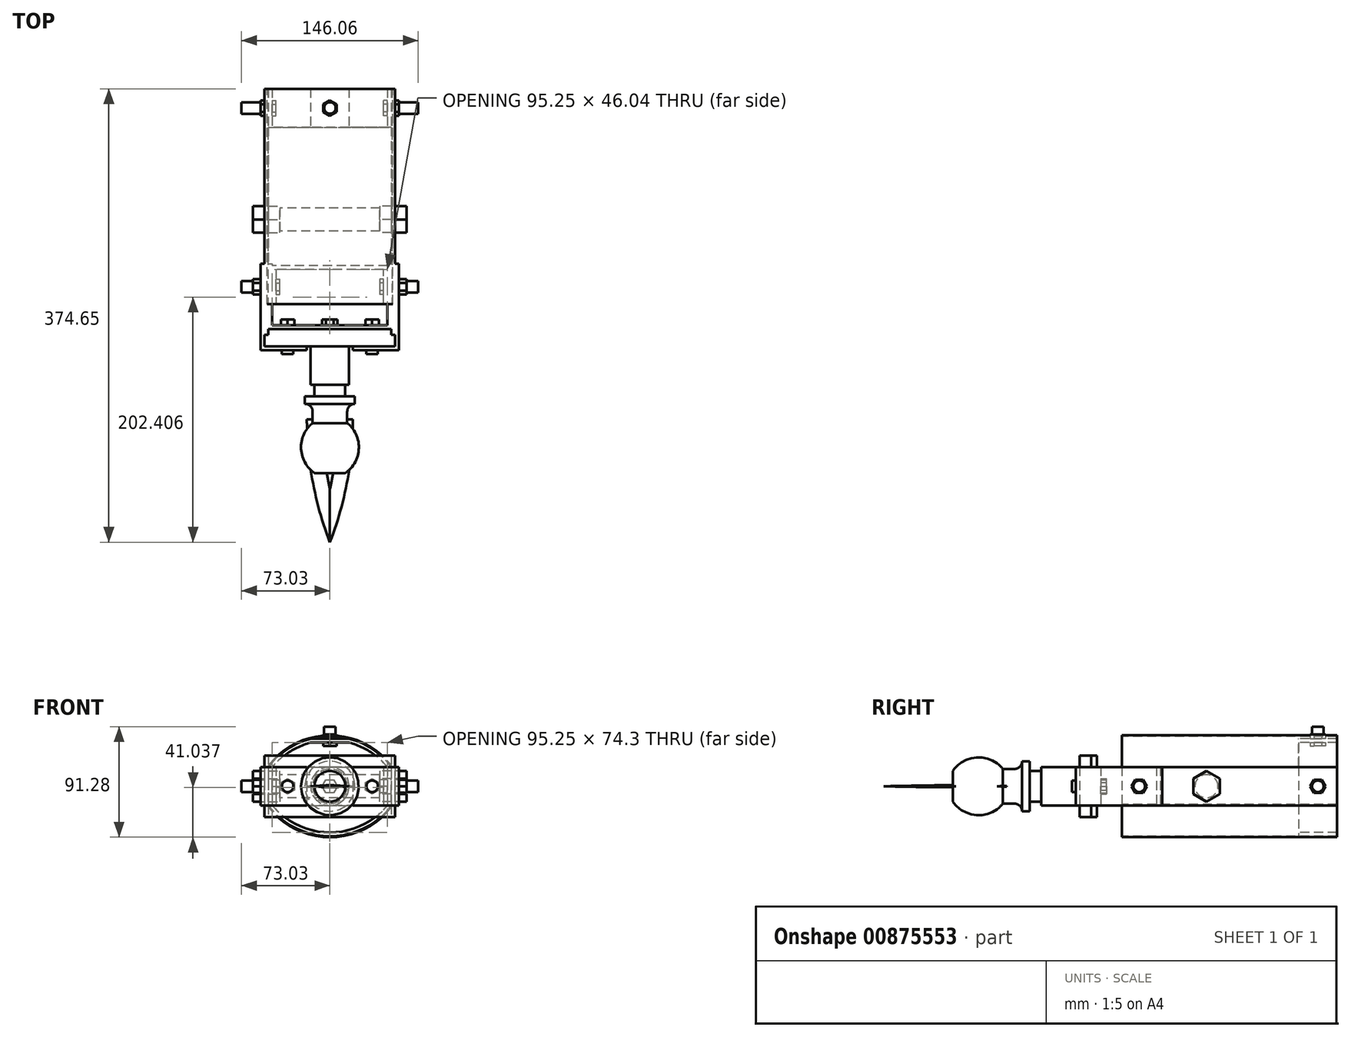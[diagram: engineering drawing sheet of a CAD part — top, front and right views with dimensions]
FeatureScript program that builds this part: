
annotation { "Feature Type Name" : "Feature", "Feature Type Description" : "" }
export const myFeature = defineFeature(function(context is Context, id is Id, definition is map)
    precondition{}
    {
        {
            var Q0;
            Q0=qCreatedBy(makeId("Right.planeOp"),FACE);
            var sketch = newSketch(context, id + "F0", { "sketchPlane" : qUnion([Q0])});
            skLineSegment(sketch, "E0.bottom", {"start": v(101.6, -15.88) * mm, "end": v(-101.6, -15.88) * mm});
            skLineSegment(sketch, "E0.top", {"start": v(101.6, 15.88) * mm, "end": v(-101.6, 15.88) * mm});
            skLineSegment(sketch, "E0.left", {"start": v(101.6, -15.88) * mm, "end": v(101.6, 15.87) * mm});
            skLineSegment(sketch, "E0.right", {"start": v(-101.6, -15.88) * mm, "end": v(-101.6, 15.87) * mm});
            skPoint(sketch, "E0.middle", {"position": v(0, 0) * mm});
            skSolve(sketch);
        }
        {
            var Q0;
            Q0 = qSketchRegion(id + "F0", true);
            extrude(context, id + "F1", {"entities" : qUnion([Q0]), "depth" : 53.97 * mm, "offsetDistance" : 25.4 * mm, "hasSecondDirection" : true, "secondDirectionOppositeDirection" : false, "secondDirectionDepth" : 50.8 * mm});
        }
        {
            var Q0;
            Q0=makeQuery(id+"F0.imprint","IMPRINT",FACE,{"disambiguationData":[TD([[makeQuery(id+"F0.imprint","IMPRINT",EDGE,{"derivedFrom":sQuery(id+"F0.wireOp",EDGE,"E0.bottom")}),-1.0]])]});
            extrude(context, id + "F2", {"entities" : qUnion([Q0]), "oppositeDirection" : true, "depth" : 53.97 * mm, "offsetDistance" : 25.4 * mm, "hasSecondDirection" : true, "secondDirectionOppositeDirection" : true, "secondDirectionDepth" : 50.8 * mm});
        }
        {
            var Q0;
            Q0=qCreatedBy(makeId("Front.planeOp"),FACE);
            var sketch = newSketch(context, id + "F3", { "sketchPlane" : qUnion([Q0])});
            skLineSegment(sketch, "E1", {"start": v(50.8, 15.88) * mm, "end": v(50.8, -15.88) * mm});
            skLineSegment(sketch, "E2", {"start": v(-50.8, 15.88) * mm, "end": v(-50.8, -15.88) * mm});
            skArc(sketch, "E3", {"start": v(-50.8, 15.88) * mm, "mid": v(-35.33, 30.54) * mm, "end": v(-15.88, 39.26) * mm});
            skArc(sketch, "E4", {"start": v(50.8, -15.88) * mm, "mid": v(0, -41.28) * mm, "end": v(-50.8, -15.88) * mm});
            skLineSegment(sketch, "E5", {"start": v(-47.62, 15.88) * mm, "end": v(-47.62, -15.88) * mm});
            skLineSegment(sketch, "E6", {"start": v(47.63, 15.88) * mm, "end": v(47.63, -15.88) * mm});
            skArc(sketch, "E7", {"start": v(-47.62, 15.87) * mm, "mid": v(-33.32, 28.46) * mm, "end": v(-15.88, 36.11) * mm});
            skArc(sketch, "E8", {"start": v(47.62, -15.87) * mm, "mid": v(0, -38.18) * mm, "end": v(-47.62, -15.88) * mm});
            skLineSegment(sketch, "E9", {"start": v(15.88, 39.26) * mm, "end": v(-15.88, 39.26) * mm});
            skLineSegment(sketch, "E10", {"start": v(15.88, 36.11) * mm, "end": v(-15.88, 36.11) * mm});
            skArc(sketch, "E11.trimOffspring", {"start": v(15.88, 39.26) * mm, "mid": v(35.33, 30.54) * mm, "end": v(50.8, 15.88) * mm});
            skArc(sketch, "E12.trimOffspring", {"start": v(15.87, 36.11) * mm, "mid": v(33.32, 28.46) * mm, "end": v(47.62, 15.87) * mm});
            skLineSegment(sketch, "E13", {"start": v(15.88, 39.26) * mm, "end": v(15.88, 37.7) * mm});
            skLineSegment(sketch, "E14", {"start": v(15.88, 37.7) * mm, "end": v(-15.88, 37.7) * mm});
            skLineSegment(sketch, "E15", {"start": v(-15.88, 37.7) * mm, "end": v(-15.88, 36.11) * mm});
            skSolve(sketch);
        }
        {
            var Q0;
            Q0=makeQuery(id+"F3.imprint","IMPRINT",FACE,{"disambiguationData":[TD([[makeQuery(id+"F3.imprint","IMPRINT",EDGE,{"derivedFrom":sQuery(id+"F3.wireOp",EDGE,"E1")}),-1.0]])]});
            extrude(context, id + "F4", {"entities" : qUnion([Q0]), "operationType" : NewBodyOperationType.ADD, "oppositeDirection" : true, "depth" : 101.6 * mm, "offsetDistance" : 25.4 * mm, "hasSecondDirection" : true, "secondDirectionOppositeDirection" : true, "secondDirectionDepth" : 69.85 * mm});
        }
        {
            var Q0;
            Q0=sQuery(id+"F3.wireOp",EDGE,"E15");
            var Q1;
            Q1=sQuery(id+"F3.wireOp",EDGE,"E14");
            var Q2;
            Q2=sQuery(id+"F3.wireOp",EDGE,"E13");
            extrude(context, id + "F5", {"bodyType" : ToolBodyType.SURFACE, "surfaceEntities" : qUnion([Q0, Q1, Q2]), "oppositeDirection" : true, "depth" : 101.73 * mm, "offsetDistance" : 25.4 * mm, "hasSecondDirection" : true, "secondDirectionOppositeDirection" : true, "secondDirectionDepth" : 69.72 * mm});
        }
        {
            var Q0;
            Q0=qCreatedBy(makeId("Top.planeOp"),FACE);
            var sketch = newSketch(context, id + "F6", { "sketchPlane" : qUnion([Q0])});
            skLineSegment(sketch, "E16.bottom", {"start": v(53.97, -106.36) * mm, "end": v(-53.98, -106.36) * mm});
            skLineSegment(sketch, "E16.top", {"start": v(53.98, -42.86) * mm, "end": v(-53.98, -42.86) * mm, "construction": true});
            skLineSegment(sketch, "E16.left", {"start": v(53.98, -106.36) * mm, "end": v(53.97, -42.86) * mm});
            skLineSegment(sketch, "E16.right", {"start": v(-53.98, -106.36) * mm, "end": v(-53.98, -42.86) * mm});
            skPoint(sketch, "E16.middle", {"position": v(0, -74.61) * mm});
            skLineSegment(sketch, "E17", {"start": v(-53.98, -42.86) * mm, "end": v(-57.15, -42.86) * mm});
            skLineSegment(sketch, "E18", {"start": v(-57.15, -42.86) * mm, "end": v(-57.15, -114.3) * mm});
            skLineSegment(sketch, "E19", {"start": v(-57.15, -114.3) * mm, "end": v(-19.05, -114.3) * mm});
            skLineSegment(sketch, "E20", {"start": v(57.15, -114.3) * mm, "end": v(57.15, -42.86) * mm});
            skLineSegment(sketch, "E21", {"start": v(57.15, -42.86) * mm, "end": v(53.98, -42.86) * mm});
            skLineSegment(sketch, "E22.bottom", {"start": v(-53.98, -106.36) * mm, "end": v(53.97, -106.36) * mm});
            skLineSegment(sketch, "E22.top", {"start": v(-53.98, -101.6) * mm, "end": v(53.97, -101.6) * mm});
            skLineSegment(sketch, "E22.left", {"start": v(-53.98, -106.36) * mm, "end": v(-53.98, -101.6) * mm});
            skLineSegment(sketch, "E22.right", {"start": v(53.98, -106.36) * mm, "end": v(53.98, -101.6) * mm});
            skLineSegment(sketch, "E23.bottom", {"start": v(-50.8, -101.6) * mm, "end": v(50.8, -101.6) * mm});
            skLineSegment(sketch, "E23.top", {"start": v(-50.8, -42.86) * mm, "end": v(50.8, -42.86) * mm, "construction": true});
            skLineSegment(sketch, "E23.left", {"start": v(-50.8, -101.6) * mm, "end": v(-50.8, -42.86) * mm});
            skLineSegment(sketch, "E23.right", {"start": v(50.8, -101.6) * mm, "end": v(50.8, -42.86) * mm});
            skLineSegment(sketch, "E24", {"start": v(-50.8, -42.86) * mm, "end": v(-47.63, -42.86) * mm});
            skLineSegment(sketch, "E25", {"start": v(-47.63, -42.86) * mm, "end": v(-47.62, -93.66) * mm});
            skLineSegment(sketch, "E26", {"start": v(-47.62, -93.66) * mm, "end": v(47.63, -93.66) * mm});
            skLineSegment(sketch, "E27", {"start": v(47.63, -93.66) * mm, "end": v(47.63, -42.86) * mm});
            skLineSegment(sketch, "E28", {"start": v(47.63, -42.86) * mm, "end": v(50.8, -42.86) * mm});
            skLineSegment(sketch, "E29.top", {"start": v(-50.8, -96.84) * mm, "end": v(50.8, -96.84) * mm});
            skLineSegment(sketch, "E29.left", {"start": v(-50.8, -101.6) * mm, "end": v(-50.8, -96.84) * mm});
            skLineSegment(sketch, "E29.right", {"start": v(50.8, -101.6) * mm, "end": v(50.8, -96.84) * mm});
            skLineSegment(sketch, "E30", {"start": v(-19.05, -111.12) * mm, "end": v(-19.05, -114.3) * mm});
            skLineSegment(sketch, "E31", {"start": v(19.05, -111.12) * mm, "end": v(19.05, -114.3) * mm});
            skLineSegment(sketch, "E32.trimOffspring", {"start": v(19.05, -114.3) * mm, "end": v(57.15, -114.3) * mm});
            skLineSegment(sketch, "E33", {"start": v(-53.98, -106.36) * mm, "end": v(-53.98, -111.13) * mm});
            skLineSegment(sketch, "E34", {"start": v(-53.98, -111.13) * mm, "end": v(53.97, -111.12) * mm});
            skLineSegment(sketch, "E35", {"start": v(53.97, -111.12) * mm, "end": v(53.97, -106.36) * mm});
            skPoint(sketch, "E36.orphan", {"position": v(19.05, -106.36) * mm});
            skPoint(sketch, "E37.orphan", {"position": v(-19.05, -106.36) * mm});
            skSolve(sketch);
        }
        {
            var Q0;
            Q0=makeQuery(id+"F6.imprint","IMPRINT",FACE,{"disambiguationData":[TD([[makeQuery(id+"F6.imprint","IMPRINT",EDGE,{"derivedFrom":sQuery(id+"F6.wireOp",EDGE,"E20")}),1.0]])]});
            var Q1;
            {var subQ0=sQuery(id+"F6.wireOp",EDGE,"E24");Q1=makeQuery(id+"F6.imprint","IMPRINT",FACE,{"disambiguationData":[TD([[makeQuery(id+"F6.imprint","IMPRINT",EDGE,{"derivedFrom":subQ0}),-1.0]])]});}
            var Q2;
            {var subQ3=sQuery(id+"F6.wireOp",EDGE,"E17");Q2=makeQuery(id+"F6.imprint","IMPRINT",FACE,{"disambiguationData":[TD([[makeQuery(id+"F6.imprint","IMPRINT",EDGE,{"derivedFrom":subQ3}),1.0]])]});}
            extrude(context, id + "F7", {"entities" : qUnion([Q0, Q1, Q2]), "operationType" : NewBodyOperationType.ADD, "depth" : 15.88 * mm, "offsetDistance" : 25.4 * mm, "hasSecondDirection" : true, "secondDirectionOppositeDirection" : true, "secondDirectionDepth" : 15.88 * mm});
        }
        {
            var Q0;
            {var subQ1=sQuery(id+"F6.wireOp",EDGE,"E16.bottom");Q0=makeQuery(id+"F6.imprint","IMPRINT",FACE,{"disambiguationData":[TD([[makeQuery(id+"F6.imprint","IMPRINT",EDGE,{"derivedFrom":subQ1}),-1.0]])]});}
            extrude(context, id + "F8", {"entities" : qUnion([Q0]), "operationType" : NewBodyOperationType.ADD, "depth" : 25.4 * mm, "offsetDistance" : 25.4 * mm, "hasSecondDirection" : true, "secondDirectionOppositeDirection" : true, "secondDirectionDepth" : 25.4 * mm});
        }
        {
            var Q0;
            {var subQ5=sQuery(id+"F6.wireOp",EDGE,"E29.top");Q0=makeQuery(id+"F6.imprint","IMPRINT",FACE,{"disambiguationData":[TD([[makeQuery(id+"F6.imprint","IMPRINT",EDGE,{"derivedFrom":subQ5}),-1.0]])]});}
            extrude(context, id + "F9", {"entities" : qUnion([Q0]), "operationType" : NewBodyOperationType.ADD, "depth" : 25.4 * mm, "offsetDistance" : 25.4 * mm, "hasSecondDirection" : true, "secondDirectionOppositeDirection" : true, "secondDirectionDepth" : 25.4 * mm});
        }
        {
            var Q0;
            Q0=qCreatedBy(makeId("Right.planeOp"),FACE);
            var sketch = newSketch(context, id + "F10", { "sketchPlane" : qUnion([Q0])});
            skCircle(sketch, "E38", {"center": v(-6.35, 0) * mm, "radius": 9.53 * mm});
            skCircle(sketch, "E39", {"center": v(-6.35, 0) * mm, "radius": 12.7 * mm});
            skLineSegment(sketch, "E40", {"start": v(-17.35, 6.35) * mm, "end": v(-17.35, -6.35) * mm});
            skLineSegment(sketch, "E41", {"start": v(-17.35, -6.35) * mm, "end": v(-6.35, -12.7) * mm});
            skLineSegment(sketch, "E42", {"start": v(-6.35, -12.7) * mm, "end": v(4.65, -6.35) * mm});
            skLineSegment(sketch, "E43", {"start": v(4.65, -6.35) * mm, "end": v(4.65, 6.35) * mm});
            skLineSegment(sketch, "E44", {"start": v(4.65, 6.35) * mm, "end": v(-6.35, 12.7) * mm});
            skLineSegment(sketch, "E45", {"start": v(-6.35, 12.7) * mm, "end": v(-17.35, 6.35) * mm});
            skPoint(sketch, "E46", {"position": v(69.85, 0) * mm});
            skSolve(sketch);
        }
        {
            var Q0;
            Q0=makeQuery(id+"F10.imprint","IMPRINT",FACE,{"disambiguationData":[TD([[makeQuery(id+"F10.imprint","IMPRINT",EDGE,{"derivedFrom":sQuery(id+"F10.wireOp",EDGE,"E38")}),1.0]])]});
            extrude(context, id + "F11", {"entities" : qUnion([Q0]), "operationType" : NewBodyOperationType.REMOVE, "oppositeDirection" : true, "depth" : 76.2 * mm, "offsetDistance" : 25.4 * mm, "hasSecondDirection" : true, "secondDirectionOppositeDirection" : false, "secondDirectionDepth" : 76.2 * mm});
        }
        {
            var Q0;
            Q0=makeQuery(id+"F10.imprint","IMPRINT",FACE,{"disambiguationData":[TD([[makeQuery(id+"F10.imprint","IMPRINT",EDGE,{"derivedFrom":sQuery(id+"F10.wireOp",EDGE,"E38")}),1.0]])]});
            extrude(context, id + "F12", {"entities" : qUnion([Q0]), "operationType" : NewBodyOperationType.ADD, "depth" : 63.5 * mm, "offsetDistance" : 25.4 * mm, "hasSecondDirection" : true, "secondDirectionOppositeDirection" : true, "secondDirectionDepth" : 63.5 * mm});
        }
        {
            var Q0;
            Q0=makeQuery(id+"F10.imprint","IMPRINT",FACE,{"disambiguationData":[TD([[makeQuery(id+"F10.imprint","IMPRINT",EDGE,{"derivedFrom":sQuery(id+"F10.wireOp",EDGE,"E38")}),-1.0]])]});
            extrude(context, id + "F13", {"entities" : qUnion([Q0]), "operationType" : NewBodyOperationType.ADD, "oppositeDirection" : true, "depth" : 63.5 * mm, "offsetDistance" : 25.4 * mm, "hasSecondDirection" : true, "secondDirectionOppositeDirection" : true, "secondDirectionDepth" : 41.27 * mm});
        }
        {
            var Q0;
            Q0=makeQuery(id+"F10.imprint","IMPRINT",FACE,{"disambiguationData":[TD([[makeQuery(id+"F10.imprint","IMPRINT",EDGE,{"derivedFrom":sQuery(id+"F10.wireOp",EDGE,"E38")}),-1.0]])]});
            extrude(context, id + "F14", {"entities" : qUnion([Q0]), "operationType" : NewBodyOperationType.ADD, "depth" : 63.5 * mm, "offsetDistance" : 25.4 * mm, "hasSecondDirection" : true, "secondDirectionOppositeDirection" : false, "secondDirectionDepth" : 41.27 * mm});
        }
        {
            var Q0;
            Q0=qCreatedBy(makeId("Front.planeOp"),FACE);
            var sketch = newSketch(context, id + "F15", { "sketchPlane" : qUnion([Q0])});
            skCircle(sketch, "E47", {"center": v(0, 0) * mm, "radius": 15.88 * mm});
            skCircle(sketch, "E48", {"center": v(0, 0) * mm, "radius": 12.7 * mm});
            skCircle(sketch, "E49", {"center": v(0, 0) * mm, "radius": 4.76 * mm});
            skCircle(sketch, "E50", {"center": v(0, 0) * mm, "radius": 6.35 * mm});
            skLineSegment(sketch, "E51", {"start": v(-3.18, 5.5) * mm, "end": v(3.18, 5.5) * mm});
            skLineSegment(sketch, "E52", {"start": v(3.17, 5.5) * mm, "end": v(6.35, 0) * mm});
            skLineSegment(sketch, "E53", {"start": v(6.35, 0) * mm, "end": v(3.17, -5.5) * mm});
            skLineSegment(sketch, "E54", {"start": v(3.17, -5.5) * mm, "end": v(-3.17, -5.5) * mm});
            skLineSegment(sketch, "E55", {"start": v(-3.18, -5.5) * mm, "end": v(-6.35, 0) * mm});
            skLineSegment(sketch, "E56", {"start": v(-6.35, 0) * mm, "end": v(-3.18, 5.5) * mm});
            skSolve(sketch);
        }
        {
            var Q0;
            Q0=makeQuery(id+"F15.imprint","IMPRINT",FACE,{"disambiguationData":[TD([[makeQuery(id+"F15.imprint","IMPRINT",EDGE,{"derivedFrom":sQuery(id+"F15.wireOp",EDGE,"E47")}),1.0]])]});
            var Q1;
            Q1=makeQuery(id+"F15.imprint","IMPRINT",FACE,{"disambiguationData":[TD([[makeQuery(id+"F15.imprint","IMPRINT",EDGE,{"derivedFrom":sQuery(id+"F15.wireOp",EDGE,"E48")}),1.0]])]});
            var Q2;
            {var subQ0=sQuery(id+"F15.wireOp",EDGE,"E53");Q2=makeQuery(id+"F15.imprint","IMPRINT",FACE,{"disambiguationData":[TD([[makeQuery(id+"F15.imprint","IMPRINT",EDGE,{"derivedFrom":subQ0}),1.0]])]});}
            var Q3;
            Q3=makeQuery(id+"F15.imprint","IMPRINT",FACE,{"disambiguationData":[TD([[makeQuery(id+"F15.imprint","IMPRINT",EDGE,{"derivedFrom":sQuery(id+"F15.wireOp",EDGE,"E49")}),-1.0]])]});
            var Q4;
            Q4=makeQuery(id+"F15.imprint","IMPRINT",FACE,{"disambiguationData":[TD([[makeQuery(id+"F15.imprint","IMPRINT",EDGE,{"derivedFrom":sQuery(id+"F15.wireOp",EDGE,"E49")}),1.0]])]});
            var Q5;
            {var subQ0=sQuery(id+"F15.wireOp",EDGE,"E52");Q5=makeQuery(id+"F15.imprint","IMPRINT",FACE,{"disambiguationData":[TD([[makeQuery(id+"F15.imprint","IMPRINT",EDGE,{"derivedFrom":subQ0}),1.0]])]});}
            var Q6;
            {var subQ0=sQuery(id+"F15.wireOp",EDGE,"E54");Q6=makeQuery(id+"F15.imprint","IMPRINT",FACE,{"disambiguationData":[TD([[makeQuery(id+"F15.imprint","IMPRINT",EDGE,{"derivedFrom":subQ0}),1.0]])]});}
            var Q7;
            {var subQ0=sQuery(id+"F15.wireOp",EDGE,"E55");Q7=makeQuery(id+"F15.imprint","IMPRINT",FACE,{"disambiguationData":[TD([[makeQuery(id+"F15.imprint","IMPRINT",EDGE,{"derivedFrom":subQ0}),1.0]])]});}
            var Q8;
            {var subQ0=sQuery(id+"F15.wireOp",EDGE,"E56");Q8=makeQuery(id+"F15.imprint","IMPRINT",FACE,{"disambiguationData":[TD([[makeQuery(id+"F15.imprint","IMPRINT",EDGE,{"derivedFrom":subQ0}),1.0]])]});}
            var Q9;
            {var subQ0=sQuery(id+"F15.wireOp",EDGE,"E51");Q9=makeQuery(id+"F15.imprint","IMPRINT",FACE,{"disambiguationData":[TD([[makeQuery(id+"F15.imprint","IMPRINT",EDGE,{"derivedFrom":subQ0}),1.0]])]});}
            extrude(context, id + "F16", {"entities" : qUnion([Q0, Q1, Q2, Q3, Q4, Q5, Q6, Q7, Q8, Q9]), "operationType" : NewBodyOperationType.REMOVE, "depth" : 127 * mm, "offsetDistance" : 25.4 * mm, "hasSecondDirection" : true, "secondDirectionOppositeDirection" : false, "secondDirectionDepth" : 101.6 * mm});
        }
        {
            var Q0;
            Q0=makeQuery(id+"F15.imprint","IMPRINT",FACE,{"disambiguationData":[TD([[makeQuery(id+"F15.imprint","IMPRINT",EDGE,{"derivedFrom":sQuery(id+"F15.wireOp",EDGE,"E49")}),1.0]])]});
            extrude(context, id + "F17", {"entities" : qUnion([Q0]), "operationType" : NewBodyOperationType.REMOVE, "depth" : 127 * mm, "offsetDistance" : 25.4 * mm, "hasSecondDirection" : true, "secondDirectionOppositeDirection" : false, "secondDirectionDepth" : 88.9 * mm});
        }
        {
            var Q0;
            Q0=makeQuery(id+"F15.imprint","IMPRINT",FACE,{"disambiguationData":[TD([[makeQuery(id+"F15.imprint","IMPRINT",EDGE,{"derivedFrom":sQuery(id+"F15.wireOp",EDGE,"E47")}),1.0]])]});
            extrude(context, id + "F18", {"entities" : qUnion([Q0]), "operationType" : NewBodyOperationType.ADD, "depth" : 142.88 * mm, "offsetDistance" : 25.4 * mm, "hasSecondDirection" : true, "secondDirectionOppositeDirection" : false, "secondDirectionDepth" : 101.6 * mm});
        }
        {
            var Q0;
            {var subQ0=sQuery(id+"F15.wireOp",EDGE,"E52");Q0=makeQuery(id+"F15.imprint","IMPRINT",FACE,{"disambiguationData":[TD([[makeQuery(id+"F15.imprint","IMPRINT",EDGE,{"derivedFrom":subQ0}),1.0]])]});}
            var Q1;
            {var subQ0=sQuery(id+"F15.wireOp",EDGE,"E53");Q1=makeQuery(id+"F15.imprint","IMPRINT",FACE,{"disambiguationData":[TD([[makeQuery(id+"F15.imprint","IMPRINT",EDGE,{"derivedFrom":subQ0}),1.0]])]});}
            var Q2;
            Q2=makeQuery(id+"F15.imprint","IMPRINT",FACE,{"disambiguationData":[TD([[makeQuery(id+"F15.imprint","IMPRINT",EDGE,{"derivedFrom":sQuery(id+"F15.wireOp",EDGE,"E49")}),-1.0]])]});
            var Q3;
            {var subQ0=sQuery(id+"F15.wireOp",EDGE,"E51");Q3=makeQuery(id+"F15.imprint","IMPRINT",FACE,{"disambiguationData":[TD([[makeQuery(id+"F15.imprint","IMPRINT",EDGE,{"derivedFrom":subQ0}),1.0]])]});}
            var Q4;
            Q4=makeQuery(id+"F15.imprint","IMPRINT",FACE,{"disambiguationData":[TD([[makeQuery(id+"F15.imprint","IMPRINT",EDGE,{"derivedFrom":sQuery(id+"F15.wireOp",EDGE,"E48")}),1.0]])]});
            var Q5;
            {var subQ0=sQuery(id+"F15.wireOp",EDGE,"E56");Q5=makeQuery(id+"F15.imprint","IMPRINT",FACE,{"disambiguationData":[TD([[makeQuery(id+"F15.imprint","IMPRINT",EDGE,{"derivedFrom":subQ0}),1.0]])]});}
            var Q6;
            {var subQ0=sQuery(id+"F15.wireOp",EDGE,"E55");Q6=makeQuery(id+"F15.imprint","IMPRINT",FACE,{"disambiguationData":[TD([[makeQuery(id+"F15.imprint","IMPRINT",EDGE,{"derivedFrom":subQ0}),1.0]])]});}
            var Q7;
            {var subQ0=sQuery(id+"F15.wireOp",EDGE,"E54");Q7=makeQuery(id+"F15.imprint","IMPRINT",FACE,{"disambiguationData":[TD([[makeQuery(id+"F15.imprint","IMPRINT",EDGE,{"derivedFrom":subQ0}),1.0]])]});}
            extrude(context, id + "F19", {"entities" : qUnion([Q0, Q1, Q2, Q3, Q4, Q5, Q6, Q7]), "operationType" : NewBodyOperationType.ADD, "depth" : 107.95 * mm, "offsetDistance" : 25.4 * mm, "hasSecondDirection" : true, "secondDirectionOppositeDirection" : false, "secondDirectionDepth" : 101.6 * mm});
        }
        {
            var Q0;
            Q0=makeQuery(id+"F15.imprint","IMPRINT",FACE,{"disambiguationData":[TD([[makeQuery(id+"F15.imprint","IMPRINT",EDGE,{"derivedFrom":sQuery(id+"F15.wireOp",EDGE,"E49")}),1.0]])]});
            extrude(context, id + "F20", {"entities" : qUnion([Q0]), "operationType" : NewBodyOperationType.ADD, "depth" : 114.3 * mm, "offsetDistance" : 25.4 * mm, "hasSecondDirection" : true, "secondDirectionOppositeDirection" : false, "secondDirectionDepth" : 88.9 * mm});
        }
        {
            var Q0;
            Q0=makeQuery(id+"F15.imprint","IMPRINT",FACE,{"disambiguationData":[TD([[makeQuery(id+"F15.imprint","IMPRINT",EDGE,{"derivedFrom":sQuery(id+"F15.wireOp",EDGE,"E49")}),-1.0]])]});
            extrude(context, id + "F21", {"entities" : qUnion([Q0]), "operationType" : NewBodyOperationType.ADD, "depth" : 114.3 * mm, "offsetDistance" : 25.4 * mm, "hasSecondDirection" : true, "secondDirectionOppositeDirection" : false, "secondDirectionDepth" : 88.9 * mm});
        }
        {
            var Q0;
            Q0=qCreatedBy(makeId("Top.planeOp"),FACE);
            var sketch = newSketch(context, id + "F22", { "sketchPlane" : qUnion([Q0])});
            skLineSegment(sketch, "E57.bottom", {"start": v(47.62, -44.45) * mm, "end": v(-47.63, -44.45) * mm});
            skLineSegment(sketch, "E57.top", {"start": v(47.63, -76.2) * mm, "end": v(44.45, -76.2) * mm});
            skLineSegment(sketch, "E57.left", {"start": v(47.63, -44.45) * mm, "end": v(47.63, -76.2) * mm});
            skLineSegment(sketch, "E57.right", {"start": v(-47.63, -44.45) * mm, "end": v(-47.63, -76.2) * mm});
            skPoint(sketch, "E57.middle", {"position": v(0, -60.32) * mm});
            skLineSegment(sketch, "E58", {"start": v(44.45, -76.2) * mm, "end": v(44.45, -47.62) * mm});
            skLineSegment(sketch, "E59", {"start": v(44.45, -47.62) * mm, "end": v(-44.45, -47.63) * mm});
            skLineSegment(sketch, "E60", {"start": v(-44.45, -47.63) * mm, "end": v(-44.45, -76.2) * mm});
            skLineSegment(sketch, "E61.trimOffspring", {"start": v(-44.45, -76.2) * mm, "end": v(-47.62, -76.2) * mm});
            skSolve(sketch);
        }
        {
            var Q0;
            Q0=makeQuery(id+"F22.imprint","IMPRINT",FACE,{"disambiguationData":[TD([[makeQuery(id+"F22.imprint","IMPRINT",EDGE,{"derivedFrom":sQuery(id+"F22.wireOp",EDGE,"E57.bottom")}),1.0]])]});
            extrude(context, id + "F23", {"entities" : qUnion([Q0]), "depth" : 15.88 * mm, "offsetDistance" : 25.4 * mm, "hasSecondDirection" : true, "secondDirectionOppositeDirection" : true, "secondDirectionDepth" : 15.88 * mm});
        }
        {
            var Q0;
            Q0=qCreatedBy(makeId("Right.planeOp"),FACE);
            var sketch = newSketch(context, id + "F24", { "sketchPlane" : qUnion([Q0])});
            skPoint(sketch, "E62", {"position": v(-44.45, 0) * mm});
            skPoint(sketch, "E63", {"position": v(-76.2, 0) * mm});
            skPoint(sketch, "E64", {"position": v(-47.62, 0) * mm});
            skCircle(sketch, "E65", {"center": v(-61.91, 0) * mm, "radius": 4.76 * mm});
            skCircle(sketch, "E66", {"center": v(-61.91, 0) * mm, "radius": 6.35 * mm});
            skLineSegment(sketch, "E67", {"start": v(-65.09, 5.5) * mm, "end": v(-58.74, 5.5) * mm});
            skLineSegment(sketch, "E68", {"start": v(-58.74, 5.5) * mm, "end": v(-55.56, 0) * mm});
            skLineSegment(sketch, "E69", {"start": v(-55.56, 0) * mm, "end": v(-58.74, -5.5) * mm});
            skLineSegment(sketch, "E70", {"start": v(-58.74, -5.5) * mm, "end": v(-65.09, -5.5) * mm});
            skLineSegment(sketch, "E71", {"start": v(-65.09, -5.5) * mm, "end": v(-68.26, 0) * mm});
            skLineSegment(sketch, "E72", {"start": v(-68.26, 0) * mm, "end": v(-65.09, 5.5) * mm});
            skSolve(sketch);
        }
        {
            var Q0;
            Q0=makeQuery(id+"F24.imprint","IMPRINT",FACE,{"disambiguationData":[TD([[makeQuery(id+"F24.imprint","IMPRINT",EDGE,{"derivedFrom":sQuery(id+"F24.wireOp",EDGE,"E65")}),1.0]])]});
            extrude(context, id + "F25", {"entities" : qUnion([Q0]), "operationType" : NewBodyOperationType.ADD, "depth" : 69.85 * mm, "offsetDistance" : 25.4 * mm, "hasSecondDirection" : true, "secondDirectionOppositeDirection" : false, "secondDirectionDepth" : 41.27 * mm});
        }
        {
            var Q0;
            Q0=makeQuery(id+"F24.imprint","IMPRINT",FACE,{"disambiguationData":[TD([[makeQuery(id+"F24.imprint","IMPRINT",EDGE,{"derivedFrom":sQuery(id+"F24.wireOp",EDGE,"E65")}),1.0]])]});
            extrude(context, id + "F26", {"entities" : qUnion([Q0]), "operationType" : NewBodyOperationType.ADD, "oppositeDirection" : true, "depth" : 69.85 * mm, "offsetDistance" : 25.4 * mm, "hasSecondDirection" : true, "secondDirectionOppositeDirection" : true, "secondDirectionDepth" : 41.27 * mm});
        }
        {
            var Q0;
            Q0=makeQuery(id+"F24.imprint","IMPRINT",FACE,{"disambiguationData":[TD([[makeQuery(id+"F24.imprint","IMPRINT",EDGE,{"derivedFrom":sQuery(id+"F24.wireOp",EDGE,"E65")}),-1.0]])]});
            extrude(context, id + "F27", {"entities" : qUnion([Q0]), "operationType" : NewBodyOperationType.ADD, "depth" : 63.5 * mm, "offsetDistance" : 25.4 * mm, "hasSecondDirection" : true, "secondDirectionOppositeDirection" : false, "secondDirectionDepth" : 41.27 * mm});
        }
        {
            var Q0;
            Q0=makeQuery(id+"F24.imprint","IMPRINT",FACE,{"disambiguationData":[TD([[makeQuery(id+"F24.imprint","IMPRINT",EDGE,{"derivedFrom":sQuery(id+"F24.wireOp",EDGE,"E65")}),-1.0]])]});
            extrude(context, id + "F28", {"entities" : qUnion([Q0]), "operationType" : NewBodyOperationType.ADD, "oppositeDirection" : true, "depth" : 63.5 * mm, "offsetDistance" : 25.4 * mm, "hasSecondDirection" : true, "secondDirectionOppositeDirection" : true, "secondDirectionDepth" : 41.27 * mm});
        }
        {
            var Q0;
            Q0=qCreatedBy(makeId("Front.planeOp"),FACE);
            var sketch = newSketch(context, id + "F29", { "sketchPlane" : qUnion([Q0])});
            skCircle(sketch, "E73", {"center": v(34.93, 0) * mm, "radius": 4.76 * mm});
            skCircle(sketch, "E74", {"center": v(34.93, 0) * mm, "radius": 6.35 * mm});
            skLineSegment(sketch, "E75", {"start": v(34.92, 6.35) * mm, "end": v(40.42, 3.17) * mm});
            skLineSegment(sketch, "E76", {"start": v(40.42, 3.18) * mm, "end": v(40.42, -3.18) * mm});
            skLineSegment(sketch, "E77", {"start": v(40.42, -3.17) * mm, "end": v(34.93, -6.35) * mm});
            skLineSegment(sketch, "E78", {"start": v(34.93, -6.35) * mm, "end": v(29.43, -3.17) * mm});
            skLineSegment(sketch, "E79", {"start": v(29.43, -3.18) * mm, "end": v(29.43, 3.18) * mm});
            skLineSegment(sketch, "E80", {"start": v(29.43, 3.17) * mm, "end": v(34.93, 6.35) * mm});
            skCircle(sketch, "E81", {"center": v(-34.92, 0) * mm, "radius": 4.76 * mm});
            skCircle(sketch, "E82", {"center": v(-34.92, 0) * mm, "radius": 6.35 * mm});
            skLineSegment(sketch, "E83", {"start": v(-34.93, 6.35) * mm, "end": v(-29.43, 3.17) * mm});
            skLineSegment(sketch, "E84", {"start": v(-29.43, 3.17) * mm, "end": v(-29.43, -3.17) * mm});
            skLineSegment(sketch, "E85", {"start": v(-29.43, -3.18) * mm, "end": v(-34.92, -6.35) * mm});
            skLineSegment(sketch, "E86", {"start": v(-34.92, -6.35) * mm, "end": v(-40.42, -3.17) * mm});
            skLineSegment(sketch, "E87", {"start": v(-40.42, -3.17) * mm, "end": v(-40.42, 3.17) * mm});
            skLineSegment(sketch, "E88", {"start": v(-40.42, 3.17) * mm, "end": v(-34.93, 6.35) * mm});
            skSolve(sketch);
        }
        {
            var Q0;
            Q0=makeQuery(id+"F29.imprint","IMPRINT",FACE,{"disambiguationData":[TD([[makeQuery(id+"F29.imprint","IMPRINT",EDGE,{"derivedFrom":sQuery(id+"F29.wireOp",EDGE,"E81")}),1.0]])]});
            var Q1;
            Q1=makeQuery(id+"F29.imprint","IMPRINT",FACE,{"disambiguationData":[TD([[makeQuery(id+"F29.imprint","IMPRINT",EDGE,{"derivedFrom":sQuery(id+"F29.wireOp",EDGE,"E73")}),1.0]])]});
            extrude(context, id + "F30", {"entities" : qUnion([Q0, Q1]), "operationType" : NewBodyOperationType.ADD, "depth" : 117.47 * mm, "offsetDistance" : 25.4 * mm, "hasSecondDirection" : true, "secondDirectionOppositeDirection" : false, "secondDirectionDepth" : 88.9 * mm});
        }
        {
            var Q0;
            Q0=makeQuery(id+"F29.imprint","IMPRINT",FACE,{"disambiguationData":[TD([[makeQuery(id+"F29.imprint","IMPRINT",EDGE,{"derivedFrom":sQuery(id+"F29.wireOp",EDGE,"E73")}),-1.0]])]});
            var Q1;
            Q1=makeQuery(id+"F29.imprint","IMPRINT",FACE,{"disambiguationData":[TD([[makeQuery(id+"F29.imprint","IMPRINT",EDGE,{"derivedFrom":sQuery(id+"F29.wireOp",EDGE,"E81")}),-1.0]])]});
            extrude(context, id + "F31", {"entities" : qUnion([Q0, Q1]), "operationType" : NewBodyOperationType.ADD, "depth" : 114.3 * mm, "offsetDistance" : 25.4 * mm, "hasSecondDirection" : true, "secondDirectionOppositeDirection" : false, "secondDirectionDepth" : 88.9 * mm});
        }
        {
            var Q0;
            Q0=makeQuery(id+"F24.imprint","IMPRINT",FACE,{"disambiguationData":[TD([[makeQuery(id+"F24.imprint","IMPRINT",EDGE,{"derivedFrom":sQuery(id+"F24.wireOp",EDGE,"E65")}),1.0]])]});
            extrude(context, id + "F32", {"entities" : qUnion([Q0]), "operationType" : NewBodyOperationType.ADD, "depth" : 73.02 * mm, "offsetDistance" : 25.4 * mm, "hasSecondDirection" : true, "secondDirectionOppositeDirection" : false, "secondDirectionDepth" : 44.45 * mm});
        }
        {
            var Q0;
            Q0=makeQuery(id+"F24.imprint","IMPRINT",FACE,{"disambiguationData":[TD([[makeQuery(id+"F24.imprint","IMPRINT",EDGE,{"derivedFrom":sQuery(id+"F24.wireOp",EDGE,"E65")}),1.0]])]});
            extrude(context, id + "F33", {"entities" : qUnion([Q0]), "operationType" : NewBodyOperationType.ADD, "oppositeDirection" : true, "depth" : 73.02 * mm, "offsetDistance" : 25.4 * mm, "hasSecondDirection" : true, "secondDirectionOppositeDirection" : true, "secondDirectionDepth" : 44.45 * mm});
        }
        {
            var Q0;
            Q0=makeQuery(id+"F24.imprint","IMPRINT",FACE,{"disambiguationData":[TD([[makeQuery(id+"F24.imprint","IMPRINT",EDGE,{"derivedFrom":sQuery(id+"F24.wireOp",EDGE,"E65")}),-1.0]])]});
            extrude(context, id + "F34", {"entities" : qUnion([Q0]), "operationType" : NewBodyOperationType.ADD, "depth" : 60.32 * mm, "offsetDistance" : 25.4 * mm, "hasSecondDirection" : true, "secondDirectionOppositeDirection" : false, "secondDirectionDepth" : 44.45 * mm});
        }
        {
            var Q0;
            Q0=makeQuery(id+"F24.imprint","IMPRINT",FACE,{"disambiguationData":[TD([[makeQuery(id+"F24.imprint","IMPRINT",EDGE,{"derivedFrom":sQuery(id+"F24.wireOp",EDGE,"E65")}),-1.0]])]});
            extrude(context, id + "F35", {"entities" : qUnion([Q0]), "operationType" : NewBodyOperationType.ADD, "oppositeDirection" : true, "depth" : 60.32 * mm, "offsetDistance" : 25.4 * mm, "hasSecondDirection" : true, "secondDirectionOppositeDirection" : true, "secondDirectionDepth" : 44.45 * mm});
        }
        {
            var Q0;
            Q0=qCreatedBy(makeId("Right.planeOp"),FACE);
            var sketch = newSketch(context, id + "F36", { "sketchPlane" : qUnion([Q0])});
            skCircle(sketch, "E89", {"center": v(85.73, 0) * mm, "radius": 4.76 * mm});
            skCircle(sketch, "E90", {"center": v(85.73, 0) * mm, "radius": 6.35 * mm});
            skLineSegment(sketch, "E91", {"start": v(82.55, 5.5) * mm, "end": v(88.9, 5.5) * mm});
            skLineSegment(sketch, "E92", {"start": v(88.9, 5.5) * mm, "end": v(92.08, 0) * mm});
            skLineSegment(sketch, "E93", {"start": v(92.08, 0) * mm, "end": v(88.9, -5.5) * mm});
            skLineSegment(sketch, "E94", {"start": v(88.9, -5.5) * mm, "end": v(82.55, -5.5) * mm});
            skLineSegment(sketch, "E95", {"start": v(82.55, -5.5) * mm, "end": v(79.38, 0) * mm});
            skLineSegment(sketch, "E96", {"start": v(79.38, 0) * mm, "end": v(82.55, 5.5) * mm});
            skSolve(sketch);
        }
        {
            var Q0;
            Q0=makeQuery(id+"F36.imprint","IMPRINT",FACE,{"disambiguationData":[TD([[makeQuery(id+"F36.imprint","IMPRINT",EDGE,{"derivedFrom":sQuery(id+"F36.wireOp",EDGE,"E89")}),1.0]])]});
            extrude(context, id + "F37", {"entities" : qUnion([Q0]), "operationType" : NewBodyOperationType.ADD, "depth" : 73.02 * mm, "offsetDistance" : 25.4 * mm, "hasSecondDirection" : true, "secondDirectionOppositeDirection" : false, "secondDirectionDepth" : 44.45 * mm});
        }
        {
            var Q0;
            Q0=makeQuery(id+"F36.imprint","IMPRINT",FACE,{"disambiguationData":[TD([[makeQuery(id+"F36.imprint","IMPRINT",EDGE,{"derivedFrom":sQuery(id+"F36.wireOp",EDGE,"E89")}),1.0]])]});
            extrude(context, id + "F38", {"entities" : qUnion([Q0]), "operationType" : NewBodyOperationType.ADD, "oppositeDirection" : true, "depth" : 73.02 * mm, "offsetDistance" : 25.4 * mm, "hasSecondDirection" : true, "secondDirectionOppositeDirection" : true, "secondDirectionDepth" : 44.45 * mm});
        }
        {
            var Q0;
            Q0=makeQuery(id+"F36.imprint","IMPRINT",FACE,{"disambiguationData":[TD([[makeQuery(id+"F36.imprint","IMPRINT",EDGE,{"derivedFrom":sQuery(id+"F36.wireOp",EDGE,"E89")}),-1.0]])]});
            extrude(context, id + "F39", {"entities" : qUnion([Q0]), "operationType" : NewBodyOperationType.ADD, "depth" : 57.15 * mm, "offsetDistance" : 25.4 * mm, "hasSecondDirection" : true, "secondDirectionOppositeDirection" : false, "secondDirectionDepth" : 44.45 * mm});
        }
        {
            var Q0;
            Q0=makeQuery(id+"F36.imprint","IMPRINT",FACE,{"disambiguationData":[TD([[makeQuery(id+"F36.imprint","IMPRINT",EDGE,{"derivedFrom":sQuery(id+"F36.wireOp",EDGE,"E89")}),-1.0]])]});
            extrude(context, id + "F40", {"entities" : qUnion([Q0]), "operationType" : NewBodyOperationType.ADD, "oppositeDirection" : true, "depth" : 57.15 * mm, "offsetDistance" : 25.4 * mm, "hasSecondDirection" : true, "secondDirectionOppositeDirection" : true, "secondDirectionDepth" : 44.45 * mm});
        }
        {
            var Q0;
            Q0=qCreatedBy(makeId("Top.planeOp"),FACE);
            var sketch = newSketch(context, id + "F41", { "sketchPlane" : qUnion([Q0])});
            skCircle(sketch, "E97", {"center": v(0, 85.73) * mm, "radius": 4.76 * mm});
            skCircle(sketch, "E98", {"center": v(0, 85.73) * mm, "radius": 6.35 * mm});
            skLineSegment(sketch, "E99", {"start": v(0, 92.08) * mm, "end": v(5.5, 88.9) * mm});
            skLineSegment(sketch, "E100", {"start": v(5.5, 88.9) * mm, "end": v(5.5, 82.55) * mm});
            skLineSegment(sketch, "E101", {"start": v(5.5, 82.55) * mm, "end": v(0, 79.38) * mm});
            skLineSegment(sketch, "E102", {"start": v(0, 79.38) * mm, "end": v(-5.5, 82.55) * mm});
            skLineSegment(sketch, "E103", {"start": v(-5.5, 82.55) * mm, "end": v(-5.5, 88.9) * mm});
            skLineSegment(sketch, "E104", {"start": v(-5.5, 88.9) * mm, "end": v(0, 92.08) * mm});
            skSolve(sketch);
        }
        {
            var Q0;
            Q0=makeQuery(id+"F41.imprint","IMPRINT",FACE,{"disambiguationData":[TD([[makeQuery(id+"F41.imprint","IMPRINT",EDGE,{"derivedFrom":sQuery(id+"F41.wireOp",EDGE,"E97")}),1.0]])]});
            extrude(context, id + "F42", {"entities" : qUnion([Q0]), "operationType" : NewBodyOperationType.ADD, "depth" : 49.2 * mm, "offsetDistance" : 25.4 * mm, "hasSecondDirection" : true, "secondDirectionOppositeDirection" : false, "secondDirectionDepth" : 33.34 * mm});
        }
        {
            var Q0;
            Q0=makeQuery(id+"F41.imprint","IMPRINT",FACE,{"disambiguationData":[TD([[makeQuery(id+"F41.imprint","IMPRINT",EDGE,{"derivedFrom":sQuery(id+"F41.wireOp",EDGE,"E97")}),-1.0]])]});
            extrude(context, id + "F43", {"entities" : qUnion([Q0]), "operationType" : NewBodyOperationType.ADD, "depth" : 42.86 * mm, "offsetDistance" : 25.4 * mm, "hasSecondDirection" : true, "secondDirectionOppositeDirection" : false, "secondDirectionDepth" : 33.34 * mm});
        }
        {
            var Q0;
            Q0=qCreatedBy(makeId("Top.planeOp"),FACE);
            var sketch = newSketch(context, id + "F44", { "sketchPlane" : qUnion([Q0])});
            skLineSegment(sketch, "E105", {"start": v(-12.7, -107.95) * mm, "end": v(12.7, -107.95) * mm});
            skLineSegment(sketch, "E106", {"start": v(0, -107.95) * mm, "end": v(0, -152.4) * mm});
            skLineSegment(sketch, "E107", {"start": v(12.7, -107.95) * mm, "end": v(12.7, -152.4) * mm});
            skLineSegment(sketch, "E108", {"start": v(12.7, -152.4) * mm, "end": v(0, -152.4) * mm});
            skLineSegment(sketch, "E109", {"start": v(0, -152.4) * mm, "end": v(0, -215.9) * mm});
            skLineSegment(sketch, "E110", {"start": v(0, -215.9) * mm, "end": v(12.7, -215.9) * mm});
            skLineSegment(sketch, "E111", {"start": v(0, -152.4) * mm, "end": v(20.64, -152.4) * mm});
            skLineSegment(sketch, "E112", {"start": v(20.64, -152.4) * mm, "end": v(20.64, -158.75) * mm});
            skPoint(sketch, "E113", {"position": v(23.81, -196.85) * mm});
            skLineSegment(sketch, "E114", {"start": v(12.7, -215.9) * mm, "end": v(12.7, -158.75) * mm, "construction": true});
            skArc(sketch, "E115", {"start": v(20.64, -158.75) * mm, "mid": v(16.15, -160.6) * mm, "end": v(14.29, -165.1) * mm});
            skLineSegment(sketch, "E116", {"start": v(14.29, -165.1) * mm, "end": v(14.29, -174.62) * mm});
            skArc(sketch, "E117", {"start": v(12.7, -215.9) * mm, "mid": v(23.89, -195.66) * mm, "end": v(14.29, -174.62) * mm});
            skSolve(sketch);
        }
        {
            var Q0;
            {var subQ0=sQuery(id+"F44.wireOp",EDGE,"E106");Q0=makeQuery(id+"F44.imprint","IMPRINT",FACE,{"disambiguationData":[TD([[makeQuery(id+"F44.imprint","IMPRINT",EDGE,{"derivedFrom":subQ0}),1.0]])]});}
            var Q1;
            Q1=makeQuery(id+"F44.imprint","IMPRINT",FACE,{"disambiguationData":[TD([[makeQuery(id+"F44.imprint","IMPRINT",EDGE,{"derivedFrom":sQuery(id+"F44.wireOp",EDGE,"E108")}),1.0]])]});
            var Q2;
            Q2=sQuery(id+"F44.wireOp",EDGE,"E109");
            revolve(context, id + "F45", {"surfaceOperationType" : NewSurfaceOperationType.NEW, "entities" : qUnion([Q0, Q1]), "axis" : qUnion([Q2]), "revolveType" : RevolveType.FULL});
        }
        {
            var Q0;
            Q0=qCreatedBy(makeId("Top.planeOp"),FACE);
            var sketch = newSketch(context, id + "F46", { "sketchPlane" : qUnion([Q0])});
            skLineSegment(sketch, "E118.bottom", {"start": v(0, -107.95) * mm, "end": v(12.7, -107.95) * mm});
            skLineSegment(sketch, "E118.top", {"start": v(0, -158.75) * mm, "end": v(12.7, -158.75) * mm});
            skLineSegment(sketch, "E118.left", {"start": v(0, -107.95) * mm, "end": v(0, -158.75) * mm});
            skLineSegment(sketch, "E118.right", {"start": v(12.7, -107.95) * mm, "end": v(12.7, -158.75) * mm});
            skLineSegment(sketch, "E119.bottom", {"start": v(0, -158.75) * mm, "end": v(9.53, -158.75) * mm});
            skLineSegment(sketch, "E119.left", {"start": v(0, -158.75) * mm, "end": v(0, -209.55) * mm});
            skLineSegment(sketch, "E119.right", {"start": v(9.53, -158.75) * mm, "end": v(9.53, -171.45) * mm});
            skLineSegment(sketch, "E120", {"start": v(9.53, -171.45) * mm, "end": v(0, -209.55) * mm});
            skPoint(sketch, "E119.top.end.orphan", {"position": v(9.53, -209.55) * mm});
            skSolve(sketch);
        }
        {
            var Q0;
            Q0=makeQuery(id+"F46.imprint","IMPRINT",FACE,{"disambiguationData":[TD([[makeQuery(id+"F46.imprint","IMPRINT",EDGE,{"derivedFrom":sQuery(id+"F46.wireOp",EDGE,"E118.bottom")}),-1.0]])]});
            var Q1;
            {var subQ0=sQuery(id+"F46.wireOp",EDGE,"E119.left");Q1=makeQuery(id+"F46.imprint","IMPRINT",FACE,{"disambiguationData":[TD([[makeQuery(id+"F46.imprint","IMPRINT",EDGE,{"derivedFrom":subQ0}),1.0]])]});}
            var Q2;
            Q2=sQuery(id+"F46.wireOp",EDGE,"E118.left");
            revolve(context, id + "F47", {"surfaceOperationType" : NewSurfaceOperationType.NEW, "entities" : qUnion([Q0, Q1]), "axis" : qUnion([Q2]), "revolveType" : RevolveType.FULL});
        }
        {
            var Q0;
            Q0=qCreatedBy(makeId("Top.planeOp"),FACE);
            var sketch = newSketch(context, id + "F48", { "sketchPlane" : qUnion([Q0])});
            skLineSegment(sketch, "E121.bottom", {"start": v(12.7, -158.75) * mm, "end": v(-12.7, -158.75) * mm});
            skLineSegment(sketch, "E121.top", {"start": v(12.7, -107.95) * mm, "end": v(-12.7, -107.95) * mm});
            skLineSegment(sketch, "E121.left", {"start": v(12.7, -158.75) * mm, "end": v(12.7, -107.95) * mm});
            skLineSegment(sketch, "E121.right", {"start": v(-12.7, -158.75) * mm, "end": v(-12.7, -107.95) * mm});
            skPoint(sketch, "E121.middle", {"position": v(0, -133.35) * mm});
            skLineSegment(sketch, "E122.bottom", {"start": v(9.53, -158.75) * mm, "end": v(-9.52, -158.75) * mm});
            skLineSegment(sketch, "E122.top", {"start": v(9.53, -184.15) * mm, "end": v(-9.52, -184.15) * mm});
            skLineSegment(sketch, "E122.left", {"start": v(9.53, -158.75) * mm, "end": v(9.53, -184.15) * mm});
            skLineSegment(sketch, "E122.right", {"start": v(-9.52, -158.75) * mm, "end": v(-9.52, -184.15) * mm});
            skPoint(sketch, "E122.middle", {"position": v(0, -171.45) * mm});
            skLineSegment(sketch, "E123.bottom", {"start": v(19.05, -171.45) * mm, "end": v(-19.05, -171.45) * mm});
            skLineSegment(sketch, "E123.top", {"start": v(19.05, -273.05) * mm, "end": v(-19.05, -273.05) * mm, "construction": true});
            skLineSegment(sketch, "E123.left", {"start": v(19.05, -171.45) * mm, "end": v(19.05, -273.05) * mm, "construction": true});
            skLineSegment(sketch, "E123.right", {"start": v(-19.05, -171.45) * mm, "end": v(-19.05, -273.05) * mm, "construction": true});
            skPoint(sketch, "E123.middle", {"position": v(0, -222.25) * mm});
            skArc(sketch, "E124", {"start": v(-19.05, -171.45) * mm, "mid": v(-14.25, -223.14) * mm, "end": v(0, -273.05) * mm});
            skArc(sketch, "E125", {"start": v(0, -273.05) * mm, "mid": v(14.25, -223.14) * mm, "end": v(19.05, -171.45) * mm});
            skLineSegment(sketch, "E126", {"start": v(0, -184.15) * mm, "end": v(0, -107.95) * mm});
            skSolve(sketch);
        }
        {
            var Q0;
            {var subQ0=sQuery(id+"F48.wireOp",EDGE,"E122.left");var subQ1=sQuery(id+"F48.wireOp",EDGE,"E121.bottom");var subQ2=makeQuery(id+"F48.imprint","INTERSECT",VERTEX,{"derivedFrom":[subQ1,subQ0]});Q0=makeQuery(id+"F48.imprint","IMPRINT",FACE,{"disambiguationData":[TD([[makeQuery(id+"F48.imprint","IMPRINT",EDGE,{"disambiguationData":[TD([[subQ2,-1.0]])],"derivedFrom":subQ1}),1.0]])]});}
            var Q1;
            {var subQ0=sQuery(id+"F48.wireOp",EDGE,"E122.left");var subQ1=sQuery(id+"F48.wireOp",EDGE,"E122.top");var subQ2=makeQuery(id+"F48.imprint","INTERSECT",VERTEX,{"derivedFrom":[subQ1,subQ0]});Q1=makeQuery(id+"F48.imprint","IMPRINT",FACE,{"disambiguationData":[TD([[makeQuery(id+"F48.imprint","IMPRINT",EDGE,{"disambiguationData":[TD([[subQ2,-1.0]])],"derivedFrom":subQ1}),-1.0]])]});}
            var Q2;
            {var subQ0=sQuery(id+"F48.wireOp",EDGE,"E121.left");Q2=makeQuery(id+"F48.imprint","IMPRINT",FACE,{"disambiguationData":[TD([[makeQuery(id+"F48.imprint","IMPRINT",EDGE,{"derivedFrom":subQ0}),1.0]])]});}
            var Q3;
            Q3=sQuery(id+"F48.wireOp",EDGE,"E126");
            revolve(context, id + "F49", {"surfaceOperationType" : NewSurfaceOperationType.NEW, "entities" : qUnion([Q0, Q1, Q2]), "axis" : qUnion([Q3]), "revolveType" : RevolveType.FULL});
        }
        {
            var Q0;
            {var subQ10=sQuery(id+"F48.wireOp",EDGE,"E124");Q0=makeQuery(id+"F48.imprint","IMPRINT",FACE,{"disambiguationData":[TD([[makeQuery(id+"F48.imprint","IMPRINT",EDGE,{"derivedFrom":subQ10}),1.0]])]});}
            var Q1;
            {var subQ0=sQuery(id+"F48.wireOp",EDGE,"E122.left");var subQ1=sQuery(id+"F48.wireOp",EDGE,"E122.top");var subQ2=makeQuery(id+"F48.imprint","INTERSECT",VERTEX,{"derivedFrom":[subQ1,subQ0]});Q1=makeQuery(id+"F48.imprint","IMPRINT",FACE,{"disambiguationData":[TD([[makeQuery(id+"F48.imprint","IMPRINT",EDGE,{"disambiguationData":[TD([[subQ2,-1.0]])],"derivedFrom":subQ1}),-1.0]])]});}
            var Q2;
            {var subQ0=sQuery(id+"F48.wireOp",EDGE,"E122.right");var subQ1=sQuery(id+"F48.wireOp",EDGE,"E122.top");var subQ2=makeQuery(id+"F48.imprint","INTERSECT",VERTEX,{"derivedFrom":[subQ1,subQ0]});Q2=makeQuery(id+"F48.imprint","IMPRINT",FACE,{"disambiguationData":[TD([[makeQuery(id+"F48.imprint","IMPRINT",EDGE,{"disambiguationData":[TD([[subQ2,1.0]])],"derivedFrom":subQ1}),-1.0]])]});}
            extrude(context, id + "F50", {"entities" : qUnion([Q0, Q1, Q2]), "operationType" : NewBodyOperationType.ADD, "depth" : 0.8 * mm, "offsetDistance" : 25.4 * mm, "hasSecondDirection" : true, "secondDirectionOppositeDirection" : true, "secondDirectionDepth" : 0.8 * mm});
        }
        {
            var Q0;
            Q0=makeQuery(id+"F50.opExtrude","CAP_EDGE",EDGE,{"disambiguationData":[OSD([sQuery(id+"F48.wireOp",EDGE,"E124")])],"isStart":false});
            var Q1;
            Q1=makeQuery(id+"F50.opExtrude","CAP_EDGE",EDGE,{"disambiguationData":[OSD([sQuery(id+"F48.wireOp",EDGE,"E125")])],"isStart":false});
            chamfer(context, id + "F51", {"entities" : qUnion([Q0, Q1]), "chamferType" : ChamferType.TWO_OFFSETS, "width1" : 12.7 * mm, "oppositeDirection" : false, "width2" : 0.8 * mm, "tangentPropagation" : true});
        }
        {
            var Q0;
            Q0=makeQuery(id+"F50.opExtrude","CAP_EDGE",EDGE,{"disambiguationData":[OSD([sQuery(id+"F48.wireOp",EDGE,"E125")])],"isStart":true});
            var Q1;
            Q1=makeQuery(id+"F50.opExtrude","CAP_EDGE",EDGE,{"disambiguationData":[OSD([sQuery(id+"F48.wireOp",EDGE,"E124")])],"isStart":true});
            chamfer(context, id + "F52", {"entities" : qUnion([Q0, Q1]), "chamferType" : ChamferType.TWO_OFFSETS, "width1" : 0.8 * mm, "oppositeDirection" : false, "width2" : 12.7 * mm, "tangentPropagation" : true});
        }
        {
            var Q0;
            Q0=qCreatedBy(makeId("Right.planeOp"),FACE);
            var sketch = newSketch(context, id + "F53", { "sketchPlane" : qUnion([Q0])});
            skLineSegment(sketch, "E127", {"start": v(101.6, 41.28) * mm, "end": v(-76.2, 41.27) * mm});
            skLineSegment(sketch, "E128", {"start": v(-76.2, 41.27) * mm, "end": v(-76.2, 42.07) * mm});
            skLineSegment(sketch, "E129", {"start": v(-76.2, 42.07) * mm, "end": v(101.6, 42.07) * mm});
            skLineSegment(sketch, "E130", {"start": v(101.6, 42.07) * mm, "end": v(101.6, 41.28) * mm});
            skLineSegment(sketch, "E131", {"start": v(-78.97, -22.22) * mm, "end": v(115.15, -22.22) * mm});
            skSolve(sketch);
        }
        {
            var Q0;
            Q0 = qSketchRegion(id + "F53", true);
            var Q1;
            Q1=sQuery(id+"F53.wireOp",EDGE,"E131");
            revolve(context, id + "F54", {"surfaceOperationType" : NewSurfaceOperationType.NEW, "entities" : qUnion([Q0]), "axis" : qUnion([Q1]), "revolveType" : RevolveType.SYMMETRIC, "angle" : 108 * degree});
        }
        {
            var Q0;
            Q0=makeQuery(id+"F54.opRevolve","SWEPT_BODY",BODY,{"disambiguationData":[OSD([sQuery(id+"F53.wireOp",EDGE,"E127"),sQuery(id+"F53.wireOp",EDGE,"E128"),sQuery(id+"F53.wireOp",EDGE,"E129"),sQuery(id+"F53.wireOp",EDGE,"E130")])]});
            var Q1;
            Q1=qCreatedBy(makeId("Top.planeOp"),FACE);
            mirror(context, id + "F55", {"entities" : qUnion([Q0]), "mirrorPlane" : qUnion([Q1])});
        }
        {
            var Q0;
            Q0=makeQuery(id+"F6.imprint","IMPRINT",FACE,{"disambiguationData":[TD([[makeQuery(id+"F6.imprint","IMPRINT",EDGE,{"derivedFrom":sQuery(id+"F6.wireOp",EDGE,"E16.bottom")}),1.0]])]});
            extrude(context, id + "F56", {"entities" : qUnion([Q0]), "operationType" : NewBodyOperationType.ADD, "depth" : 25.4 * mm, "offsetDistance" : 25.4 * mm, "hasSecondDirection" : true, "secondDirectionOppositeDirection" : true, "secondDirectionDepth" : 25.4 * mm});
        }
    });
